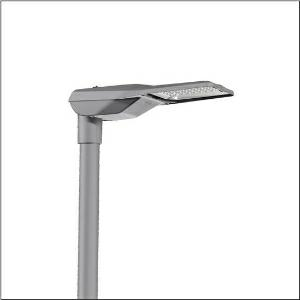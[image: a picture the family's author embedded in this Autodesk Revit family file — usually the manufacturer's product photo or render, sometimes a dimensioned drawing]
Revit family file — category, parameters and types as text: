
# Revit family: streetlight_sl_21_iq_mini___p0_8ab_5xe2r31v08hb_77c8
name_source: partatom
category: Lighting Fixtures
units: mm (PartAtom-declared; Revit-internal decimal feet)

## family parameters
Cut with Voids When Loaded = No
Host = Face
Light Source = No
Part Type = Normal
Room Calculation Point = No
Round Connector Dimension = Use Diameter
Shared = No

## types (1)
- --- (1 x LED, 8460 lm, 71 W, 3000K)
    Apparent Load = 71 VA
    CIE Flux Codes = 36 71 98 100 100
    Color Rendering = 70
    Color Temperature = 3000K
    Default Elevation = 1800 mm
    Description = Streetlight SL 21 iQ mini, mast luminaire, primary light control with lens, of PMMA, primary optical cover: cover, of toughened safety glass, transparent, light distribution: P0.8aB, light emission: direct distribution, primary light characteristic: asymmetric, installation type: post-top, side-entry, LED, High Power LED, rated luminous flux: 8.460lm, luminous efficacy: 119lm/W, light colour: 730, colour temperature: 3000K, control gear: iQ-Street Remote, D4i with power reduction, control: pre-setting: logarithmic dimming characteristic, Street-Remote, Auto-Match, Temp-Guard, Lumen-Switch, Night-Set, Smart-Wire, Light-Fading, Desk-Remote (wireless, voltage-free reading and setting of iQ features in the workshop via application-optimized NFC function/RFID function), optimised constant luminous flux control (CLO 2.0), mains connection: 220..240V, AC, 50/60Hz, start of lifetime: 71W, end of service life: 75W, reduction: 30W, luminaire housing, of diecast aluminium, powder-coated, Siteco® metallic grey (DB 702S), corrosivity category C5 mid according to DIN EN ISO 12944, please order mast flange separately, inclination adjustable: 0°, 5°, 10°, 15°, sealing non-destructively replaceable, multi-level sealing system, length: 628mm, width: 235mm, height: 110mm, mast flange for spigot size: 42mm (side-entry): 5XC10008XM4, 60/48mm (side-entry/post-top): 5XC10108XM2, 76/60mm (side-entry/post-top): 5XC10108XM1, mounting height: 4..8m, Smart Interface above, protection rating (complete): IP66, insulation class (complete): insulation class II (safety insulation), certification: CE, ENEC, ENEC+, VDE, impact resistance: IK10, permissible operating ambient temperature for outdoor applications: -40..+50°C, standard-compliant lighting for roads and squares, packaging unit: 1 piece

Light Distribution: P0.8aB
    Height = 110 mm
    Lamp = 1 x LED
    Lamp Light Flux = 8460 lm
    Lamp Power = 71 W
    Lamp count = 1
    Length = 625 mm
    Luminous efficacy = 119 lm/W
    Manufacturer = Siteco
    ModVariant = No
    Model = 5XE2R31V08HB
    Number of Poles = 1
    OnlyDefault = Yes
    Power Factor = 1
    Product Name = Streetlight SL 21 iQ mini | P0.8aB
    Product group = mast luminaire | pylon top
    ProductGroupID = 6100
    Protection Class = Protection class II
    Protection Degree = IP 66
    RLX_Detail_Level = 1
    RLX_Emergency_Light_Flux = 0 lm
    RLX_Emergency_Type = 0
    RLX_Emergency_Type_DB = No
    RlxData = <blob elided: 26113 chars, md5=976b3503>
    Socket = socket
    Standby Power = 0 W
    System Light Flux = 8460 lm
    System Power = 71 W
    Type Comments = factory setting: luminous flux: 100 % | dim-lin: 254 | 716 mA
    Type Image = l_1003515.jpg
    URL = http://relux.com
    VarID = @adj_075388
    Voltage = 0 V
    Weight = 0.00 kg
    Width = 234 mm

## geometry (parser evidence)
native form markers: Blend x4, Sweep x11
no freeform markers — native parametric forms only
